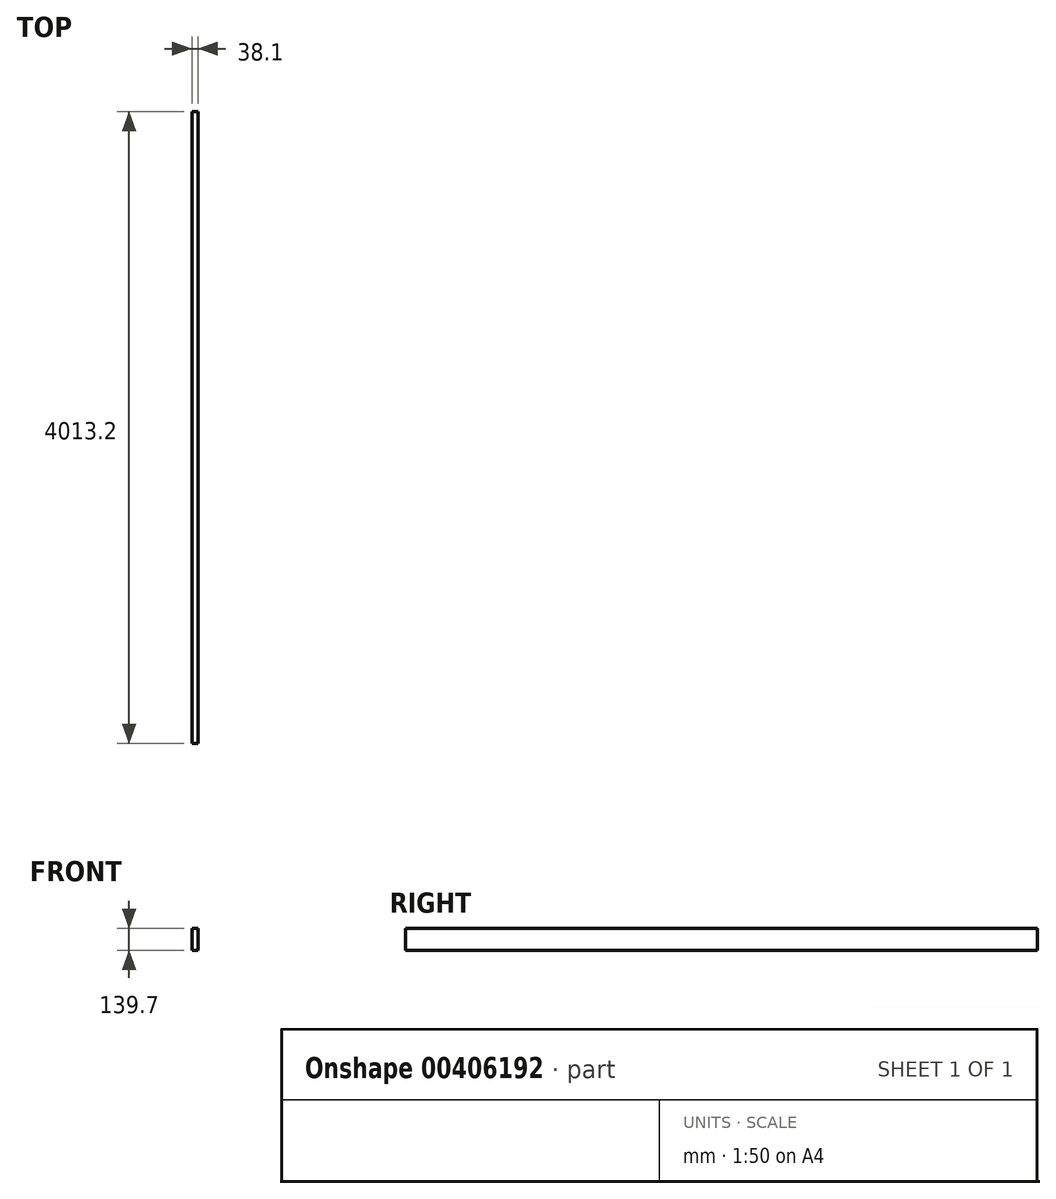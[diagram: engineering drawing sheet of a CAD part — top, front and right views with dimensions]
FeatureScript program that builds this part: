
annotation { "Feature Type Name" : "Feature", "Feature Type Description" : "" }
export const myFeature = defineFeature(function(context is Context, id is Id, definition is map)
    precondition{}
    {
        {
            var Q0;
            Q0=qCreatedBy(makeId("Front.planeOp"),FACE);
            var sketch = newSketch(context, id + "F0", { "sketchPlane" : qUnion([Q0])});
            skLineSegment(sketch, "E0.bottom", {"start": v(-19.05, -69.85) * mm, "end": v(19.05, -69.85) * mm});
            skLineSegment(sketch, "E0.top", {"start": v(-19.05, 69.85) * mm, "end": v(19.05, 69.85) * mm});
            skLineSegment(sketch, "E0.left", {"start": v(-19.05, -69.85) * mm, "end": v(-19.05, 69.85) * mm});
            skLineSegment(sketch, "E0.right", {"start": v(19.05, -69.85) * mm, "end": v(19.05, 69.85) * mm});
            skPoint(sketch, "E0.middle", {"position": v(0, 0) * mm});
            skSolve(sketch);
        }
        {
            var Q0;
            Q0=makeQuery(id+"F0.imprint","IMPRINT",FACE,{"disambiguationData":[TD([[makeQuery(id+"F0.imprint","IMPRINT",EDGE,{"derivedFrom":sQuery(id+"F0.wireOp",EDGE,"E0.bottom")}),1.0]])]});
            extrude(context, id + "F1", {"entities" : qUnion([Q0]), "oppositeDirection" : true, "depth" : 4013.2 * mm});
        }
    });
